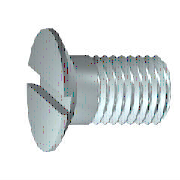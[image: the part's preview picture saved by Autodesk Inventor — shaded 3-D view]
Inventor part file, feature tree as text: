
AUTODESK INVENTOR PART (.ipt)
format: ipt  version: 2017 (Build 210142000, 142)  size: 168,960 bytes
history: native  units: mm (DEFAULTED — no unit token found)
features: sketch x2, extrude x1, plane x1
ambient origin geometry x7: Origin, YZ Plane, XZ Plane, X Axis, Y Axis, Z Axis, Center Point
bodies: Solid1 (feature_tree), Body (feature_tree)
feature tree (4):
  extrude  "Slot"  Depth=20.0mm
  plane  "Work Plane1"
  sketch  "Sketch1"  dims[d0=20.0mm d1=45.0deg d2=0.24538mm d3=18.0mm d4=1.2mm d5=1.50924mm]
  sketch  "Sketch2"  dims[d6=2.0mm d7=3.5mm d19=90.0deg d8=0.4mm d9=0.0mm d10=18.0mm d11=0.0mm d12=0.24538mm d13=0.12269mm d15=0.7mm d16=3.5mm d17=0.0mm d35=45.0deg d39=0.0mm d40=0.0mm]
